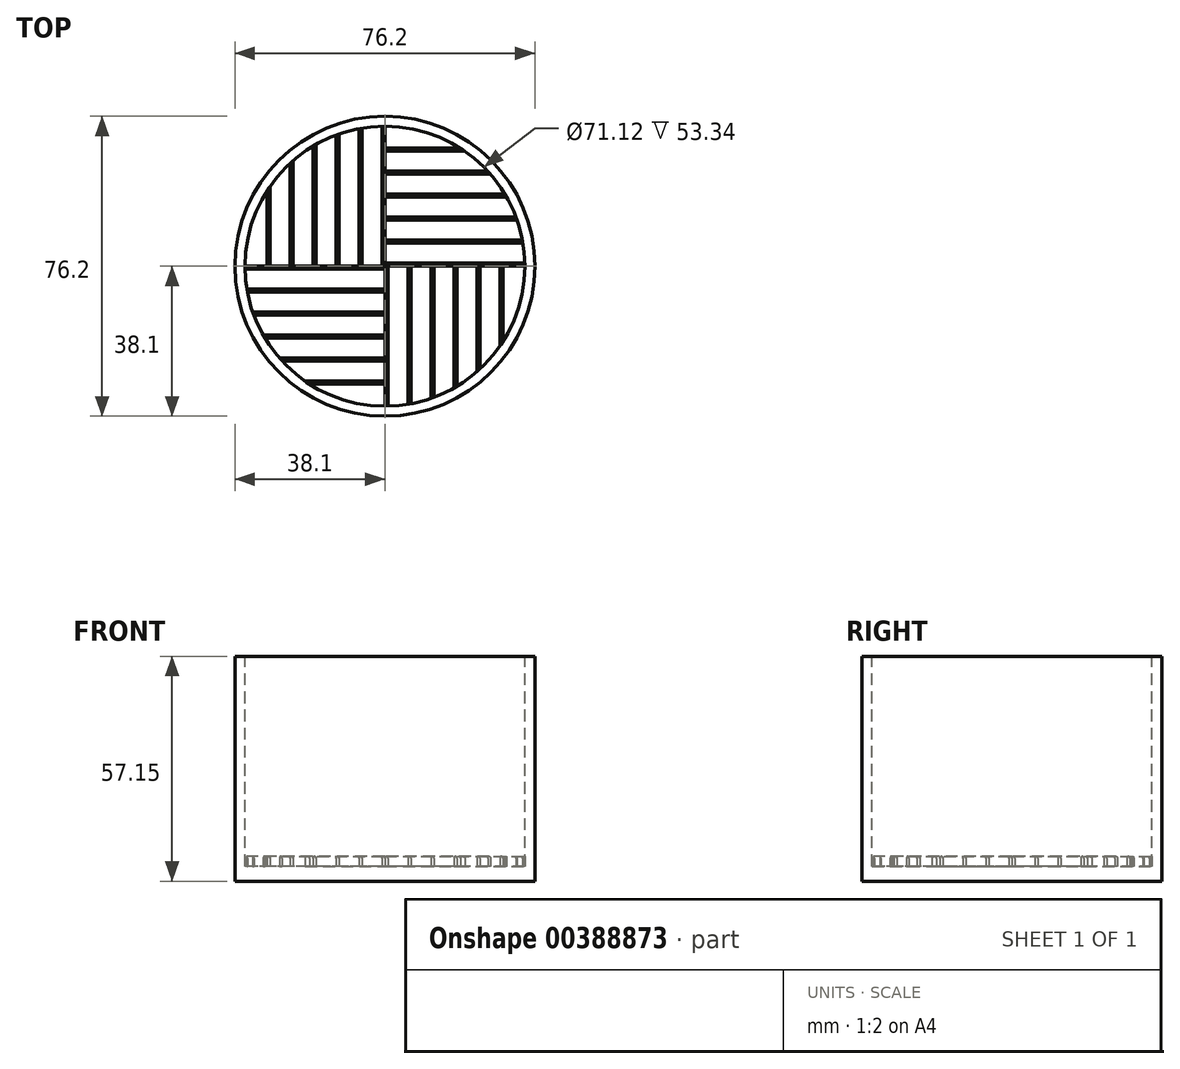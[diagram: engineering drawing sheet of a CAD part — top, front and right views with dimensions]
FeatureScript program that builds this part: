
annotation { "Feature Type Name" : "Feature", "Feature Type Description" : "" }
export const myFeature = defineFeature(function(context is Context, id is Id, definition is map)
    precondition{}
    {
        {
            var Q0;
            Q0=qCreatedBy(makeId("Top.planeOp"),FACE);
            var sketch = newSketch(context, id + "F0", { "sketchPlane" : qUnion([Q0])});
            skCircle(sketch, "E0", {"center": v(0, 0) * mm, "radius": 38.1 * mm});
            skSolve(sketch);
        }
        {
            var Q0;
            Q0 = qSketchRegion(id + "F0", true);
            extrude(context, id + "F1", {"entities" : qUnion([Q0]), "depth" : 57.15 * mm});
        }
        {
            var Q0;
            Q0=makeQuery(id+"F1.opExtrude","CAP_FACE",FACE,{"disambiguationData":[OSD([sQuery(id+"F0.wireOp",EDGE,"E0")])],"isStart":false});
            shell(context, id + "F2", {"entities" : qUnion([Q0]), "thickness" : 6.1 * mm});
        }
        {
            var Q0;
            Q0=makeQuery(id+"F1.opExtrude","CAP_FACE",FACE,{"disambiguationData":[OSD([sQuery(id+"F0.wireOp",EDGE,"E0")])],"isStart":false});
            var sketch = newSketch(context, id + "F3", { "sketchPlane" : qUnion([Q0])});
            skCircle(sketch, "E1", {"center": v(0, 0) * mm, "radius": 35.56 * mm});
            skSolve(sketch);
        }
        {
            var Q0;
            Q0 = qSketchRegion(id + "F3", true);
            extrude(context, id + "F4", {"entities" : qUnion([Q0]), "operationType" : NewBodyOperationType.REMOVE, "oppositeDirection" : true, "depth" : 53.34 * mm});
        }
        {
            var Q0;
            Q0=makeQuery(id+"F4.boolean.opBoolean","COPY",FACE,{"derivedFrom":makeQuery(id+"F4.opExtrude","CAP_FACE",FACE,{"disambiguationData":[OSD([sQuery(id+"F3.wireOp",EDGE,"E1")])],"isStart":false})});
            var sketch = newSketch(context, id + "F5", { "sketchPlane" : qUnion([Q0])});
            skLineSegment(sketch, "E2", {"start": v(0, 0) * mm, "end": v(0, 35.56) * mm});
            skLineSegment(sketch, "E3", {"start": v(0, 0.76) * mm, "end": v(35.55, 0.76) * mm});
            skLineSegment(sketch, "E4", {"start": v(0, 5.84) * mm, "end": v(35.08, 5.84) * mm});
            skLineSegment(sketch, "E5", {"start": v(0, 6.6) * mm, "end": v(34.94, 6.6) * mm});
            skLineSegment(sketch, "E6", {"start": v(0, 11.68) * mm, "end": v(33.59, 11.68) * mm});
            skLineSegment(sketch, "E7", {"start": v(0, 12.45) * mm, "end": v(33.31, 12.45) * mm});
            skLineSegment(sketch, "E8", {"start": v(0, 17.53) * mm, "end": v(30.94, 17.53) * mm});
            skLineSegment(sketch, "E9", {"start": v(0, 18.29) * mm, "end": v(30.5, 18.29) * mm});
            skLineSegment(sketch, "E10", {"start": v(0, 23.37) * mm, "end": v(26.8, 23.37) * mm});
            skLineSegment(sketch, "E11", {"start": v(0, 24.13) * mm, "end": v(26.12, 24.13) * mm});
            skLineSegment(sketch, "E12", {"start": v(20.28, 29.21) * mm, "end": v(0, 29.21) * mm});
            skLineSegment(sketch, "E13", {"start": v(0, 29.97) * mm, "end": v(19.14, 29.97) * mm});
            skLineSegment(sketch, "E14", {"start": v(0, 0) * mm, "end": v(35.56, 0) * mm});
            skSolve(sketch);
        }
        {
            var Q0;
            {var subQ0=sQuery(id+"F5.wireOp",EDGE,"E8");Q0=makeQuery(id+"F5.imprint","IMPRINT",FACE,{"disambiguationData":[TD([[makeQuery(id+"F5.imprint","IMPRINT",EDGE,{"derivedFrom":subQ0}),1.0]])]});}
            var Q1;
            {var subQ0=sQuery(id+"F5.wireOp",EDGE,"E10");Q1=makeQuery(id+"F5.imprint","IMPRINT",FACE,{"disambiguationData":[TD([[makeQuery(id+"F5.imprint","IMPRINT",EDGE,{"derivedFrom":subQ0}),1.0]])]});}
            var Q2;
            {var subQ0=sQuery(id+"F5.wireOp",EDGE,"E12");Q2=makeQuery(id+"F5.imprint","IMPRINT",FACE,{"disambiguationData":[TD([[makeQuery(id+"F5.imprint","IMPRINT",EDGE,{"derivedFrom":subQ0}),-1.0]])]});}
            var Q3;
            {var subQ0=sQuery(id+"F5.wireOp",EDGE,"E6");Q3=makeQuery(id+"F5.imprint","IMPRINT",FACE,{"disambiguationData":[TD([[makeQuery(id+"F5.imprint","IMPRINT",EDGE,{"derivedFrom":subQ0}),1.0]])]});}
            var Q4;
            {var subQ0=sQuery(id+"F5.wireOp",EDGE,"E4");Q4=makeQuery(id+"F5.imprint","IMPRINT",FACE,{"disambiguationData":[TD([[makeQuery(id+"F5.imprint","IMPRINT",EDGE,{"derivedFrom":subQ0}),1.0]])]});}
            var Q5;
            {var subQ2=sQuery(id+"F5.wireOp",EDGE,"E3");Q5=makeQuery(id+"F5.imprint","IMPRINT",FACE,{"disambiguationData":[TD([[makeQuery(id+"F5.imprint","IMPRINT",EDGE,{"derivedFrom":subQ2}),-1.0]])]});}
            extrude(context, id + "F6", {"entities" : qUnion([Q0, Q1, Q2, Q3, Q4, Q5]), "depth" : 2.54 * mm});
        }
        {
            var Q0;
            Q0=makeQuery(id+"F6.opExtrude","CAP_EDGE",EDGE,{"disambiguationData":[OSD([sQuery(id+"F5.wireOp",EDGE,"E13")])],"isStart":false});
            var Q1;
            Q1=makeQuery(id+"F6.opExtrude","CAP_EDGE",EDGE,{"disambiguationData":[OSD([sQuery(id+"F5.wireOp",EDGE,"E12")])],"isStart":false});
            var Q2;
            Q2=makeQuery(id+"F6.opExtrude","CAP_EDGE",EDGE,{"disambiguationData":[OSD([sQuery(id+"F5.wireOp",EDGE,"E10")])],"isStart":false});
            var Q3;
            Q3=makeQuery(id+"F6.opExtrude","CAP_EDGE",EDGE,{"disambiguationData":[OSD([sQuery(id+"F5.wireOp",EDGE,"E11")])],"isStart":false});
            var Q4;
            Q4=makeQuery(id+"F6.opExtrude","CAP_EDGE",EDGE,{"disambiguationData":[OSD([sQuery(id+"F5.wireOp",EDGE,"E9")])],"isStart":false});
            var Q5;
            Q5=makeQuery(id+"F6.opExtrude","CAP_EDGE",EDGE,{"disambiguationData":[OSD([sQuery(id+"F5.wireOp",EDGE,"E8")])],"isStart":false});
            var Q6;
            Q6=makeQuery(id+"F6.opExtrude","CAP_EDGE",EDGE,{"disambiguationData":[OSD([sQuery(id+"F5.wireOp",EDGE,"E7")])],"isStart":false});
            var Q7;
            Q7=makeQuery(id+"F6.opExtrude","CAP_EDGE",EDGE,{"disambiguationData":[OSD([sQuery(id+"F5.wireOp",EDGE,"E6")])],"isStart":false});
            var Q8;
            Q8=makeQuery(id+"F6.opExtrude","CAP_EDGE",EDGE,{"disambiguationData":[OSD([sQuery(id+"F5.wireOp",EDGE,"E5")])],"isStart":false});
            var Q9;
            Q9=makeQuery(id+"F6.opExtrude","CAP_EDGE",EDGE,{"disambiguationData":[OSD([sQuery(id+"F5.wireOp",EDGE,"E4")])],"isStart":false});
            var Q10;
            Q10=makeQuery(id+"F6.opExtrude","CAP_EDGE",EDGE,{"disambiguationData":[OSD([sQuery(id+"F5.wireOp",EDGE,"E3")])],"isStart":false});
            var Q11;
            Q11=makeQuery(id+"F6.opExtrude","CAP_EDGE",EDGE,{"disambiguationData":[OSD([sQuery(id+"F5.wireOp",EDGE,"E14")])],"isStart":false});
            fillet(context, id + "F7", {"entities" : qUnion([Q0, Q1, Q2, Q3, Q4, Q5, Q6, Q7, Q8, Q9, Q10, Q11]), "radius" : 0.5 * mm, "tangentPropagation" : true, "allowEdgeOverflow" : false});
        }
        {
            var Q0;
            Q0=makeQuery(id+"F6.opExtrude","SWEPT_BODY",BODY,{"disambiguationData":[OSD([sQuery(id+"F3.wireOp",EDGE,"E1"),sQuery(id+"F5.wireOp",EDGE,"E2"),sQuery(id+"F5.wireOp",EDGE,"E3"),sQuery(id+"F5.wireOp",EDGE,"E14")])]});
            var Q1;
            Q1=makeQuery(id+"F6.opExtrude","SWEPT_BODY",BODY,{"disambiguationData":[OSD([sQuery(id+"F3.wireOp",EDGE,"E1"),sQuery(id+"F5.wireOp",EDGE,"E2"),sQuery(id+"F5.wireOp",EDGE,"E4"),sQuery(id+"F5.wireOp",EDGE,"E5")])]});
            var Q2;
            Q2=makeQuery(id+"F6.opExtrude","SWEPT_BODY",BODY,{"disambiguationData":[OSD([sQuery(id+"F3.wireOp",EDGE,"E1"),sQuery(id+"F5.wireOp",EDGE,"E2"),sQuery(id+"F5.wireOp",EDGE,"E6"),sQuery(id+"F5.wireOp",EDGE,"E7")])]});
            var Q3;
            Q3=makeQuery(id+"F6.opExtrude","SWEPT_BODY",BODY,{"disambiguationData":[OSD([sQuery(id+"F3.wireOp",EDGE,"E1"),sQuery(id+"F5.wireOp",EDGE,"E2"),sQuery(id+"F5.wireOp",EDGE,"E8"),sQuery(id+"F5.wireOp",EDGE,"E9")])]});
            var Q4;
            Q4=makeQuery(id+"F6.opExtrude","SWEPT_BODY",BODY,{"disambiguationData":[OSD([sQuery(id+"F3.wireOp",EDGE,"E1"),sQuery(id+"F5.wireOp",EDGE,"E2"),sQuery(id+"F5.wireOp",EDGE,"E10"),sQuery(id+"F5.wireOp",EDGE,"E11")])]});
            var Q5;
            Q5=makeQuery(id+"F6.opExtrude","SWEPT_BODY",BODY,{"disambiguationData":[OSD([sQuery(id+"F3.wireOp",EDGE,"E1"),sQuery(id+"F5.wireOp",EDGE,"E2"),sQuery(id+"F5.wireOp",EDGE,"E12"),sQuery(id+"F5.wireOp",EDGE,"E13")])]});
            var Q6;
            Q6=makeQuery(id+"F4.boolean.opBoolean","COPY",EDGE,{"derivedFrom":makeQuery(id+"F4.opExtrude","CAP_EDGE",EDGE,{"disambiguationData":[OSD([sQuery(id+"F3.wireOp",EDGE,"E1")])],"isStart":false})});
            circularPattern(context, id + "F8", {"entities" : qUnion([Q0, Q1, Q2, Q3, Q4, Q5]), "axis" : qUnion([Q6]), "angle" : 360 * degree, "instanceCount" : 4, "equalSpace" : true});
        }
    });
